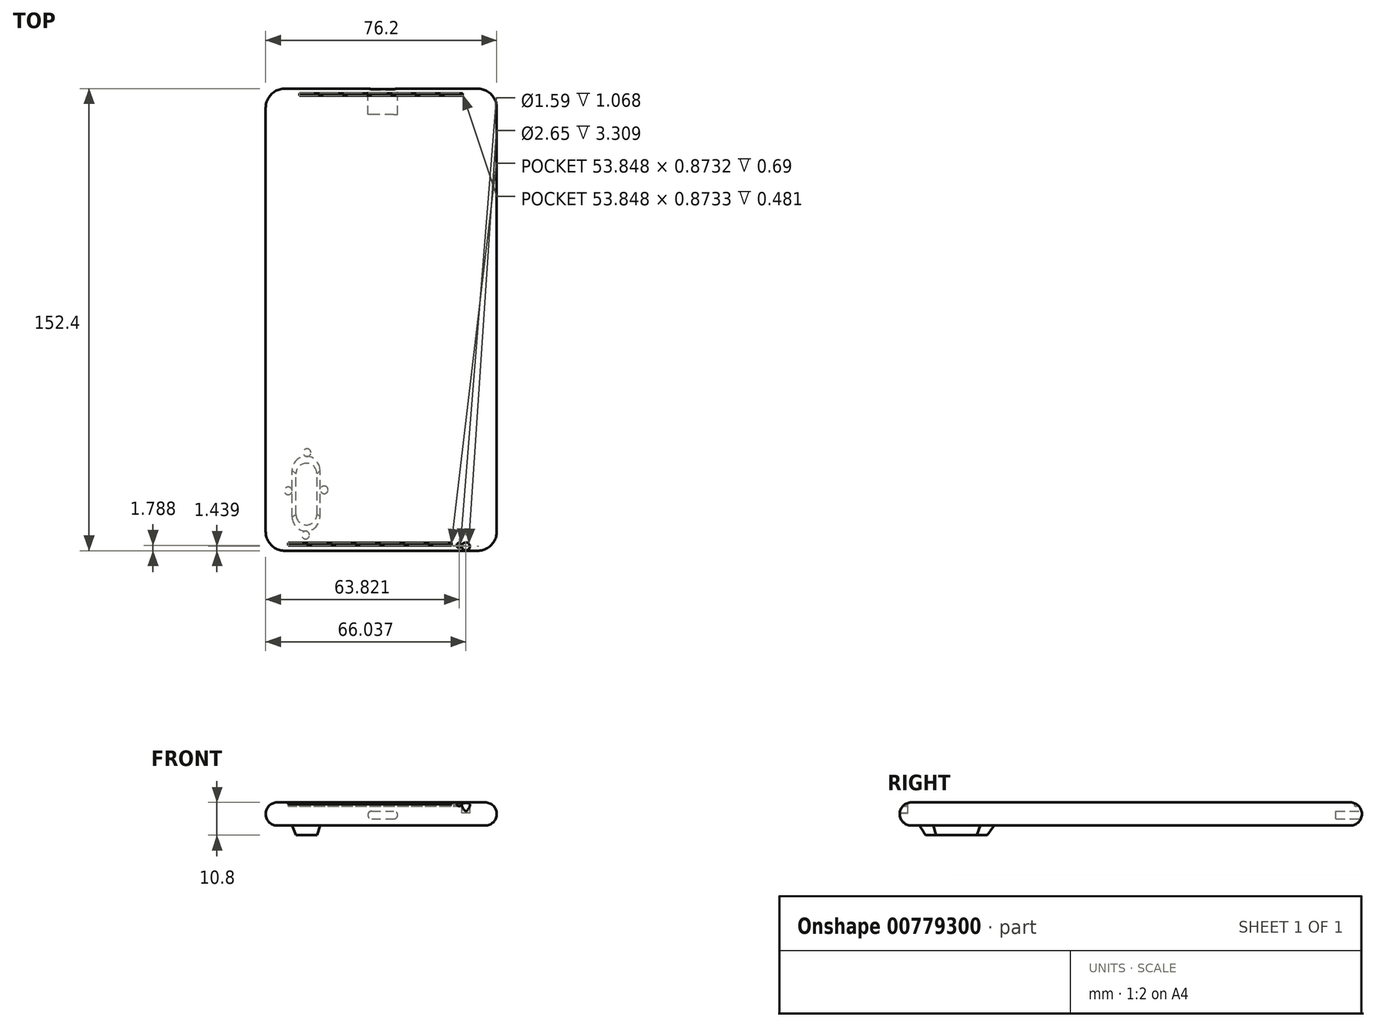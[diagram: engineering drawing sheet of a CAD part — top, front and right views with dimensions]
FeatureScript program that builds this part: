
annotation { "Feature Type Name" : "Feature", "Feature Type Description" : "" }
export const myFeature = defineFeature(function(context is Context, id is Id, definition is map)
    precondition{}
    {
        {
            var Q0;
            Q0=qCreatedBy(makeId("Top.planeOp"),FACE);
            var sketch = newSketch(context, id + "F0", { "sketchPlane" : qUnion([Q0])});
            skLineSegment(sketch, "E0.bottom", {"start": v(-50.31, -88.44) * mm, "end": v(25.89, -88.44) * mm});
            skLineSegment(sketch, "E0.top", {"start": v(-50.31, 63.96) * mm, "end": v(25.89, 63.96) * mm});
            skLineSegment(sketch, "E0.left", {"start": v(-50.31, -88.44) * mm, "end": v(-50.31, 63.96) * mm});
            skLineSegment(sketch, "E0.right", {"start": v(25.89, -88.44) * mm, "end": v(25.89, 63.96) * mm});
            skSolve(sketch);
        }
        {
            var Q0;
            Q0 = qSketchRegion(id + "F0", true);
            extrude(context, id + "F1", {"entities" : qUnion([Q0]), "depth" : 7.62 * mm, "offsetDistance" : 25.4 * mm});
        }
        {
            var Q0;
            Q0=makeQuery(id+"F1.opExtrude","CAP_FACE",FACE,{"disambiguationData":[OSD([sQuery(id+"F0.wireOp",EDGE,"E0.bottom"),sQuery(id+"F0.wireOp",EDGE,"E0.top"),sQuery(id+"F0.wireOp",EDGE,"E0.left"),sQuery(id+"F0.wireOp",EDGE,"E0.right")])],"isStart":false});
            var sketch = newSketch(context, id + "F2", { "sketchPlane" : qUnion([Q0])});
            skCircle(sketch, "E1", {"center": v(-43.96, 57.6) * mm, "radius": 6.35 * mm});
            skCircle(sketch, "E2", {"center": v(19.54, 57.6) * mm, "radius": 6.35 * mm});
            skCircle(sketch, "E3", {"center": v(-43.96, -82.1) * mm, "radius": 6.35 * mm});
            skCircle(sketch, "E4", {"center": v(19.54, -82.1) * mm, "radius": 6.35 * mm});
            skSolve(sketch);
        }
        {
            var Q0;
            {var subQ0=sQuery(id+"F2.wireOp",EDGE,"E4");var subQ1=makeQuery(id+"F1.opExtrude","CAP_EDGE",EDGE,{"disambiguationData":[OSD([sQuery(id+"F0.wireOp",EDGE,"E0.bottom")])],"isStart":false});var subQ2=makeQuery(id+"F2.imprint","INTERSECT",VERTEX,{"derivedFrom":[subQ1,subQ0]});Q0=makeQuery(id+"F2.imprint","IMPRINT",FACE,{"disambiguationData":[TD([[makeQuery(id+"F2.imprint","IMPRINT",EDGE,{"disambiguationData":[TD([[subQ2,-1.0]])],"derivedFrom":subQ0}),-1.0]])]});}
            var Q1;
            {var subQ0=sQuery(id+"F2.wireOp",EDGE,"E3");var subQ1=makeQuery(id+"F1.opExtrude","CAP_EDGE",EDGE,{"disambiguationData":[OSD([sQuery(id+"F0.wireOp",EDGE,"E0.bottom")])],"isStart":false});var subQ2=makeQuery(id+"F2.imprint","INTERSECT",VERTEX,{"derivedFrom":[subQ1,subQ0]});Q1=makeQuery(id+"F2.imprint","IMPRINT",FACE,{"disambiguationData":[TD([[makeQuery(id+"F2.imprint","IMPRINT",EDGE,{"disambiguationData":[TD([[subQ2,1.0]])],"derivedFrom":subQ0}),-1.0]])]});}
            var Q2;
            {var subQ0=sQuery(id+"F2.wireOp",EDGE,"E1");var subQ1=makeQuery(id+"F1.opExtrude","CAP_EDGE",EDGE,{"disambiguationData":[OSD([sQuery(id+"F0.wireOp",EDGE,"E0.top")])],"isStart":false});var subQ2=makeQuery(id+"F2.imprint","INTERSECT",VERTEX,{"derivedFrom":[subQ1,subQ0]});Q2=makeQuery(id+"F2.imprint","IMPRINT",FACE,{"disambiguationData":[TD([[makeQuery(id+"F2.imprint","IMPRINT",EDGE,{"disambiguationData":[TD([[subQ2,-1.0]])],"derivedFrom":subQ0}),-1.0]])]});}
            var Q3;
            {var subQ0=sQuery(id+"F2.wireOp",EDGE,"E2");var subQ1=makeQuery(id+"F1.opExtrude","CAP_EDGE",EDGE,{"disambiguationData":[OSD([sQuery(id+"F0.wireOp",EDGE,"E0.top")])],"isStart":false});var subQ2=makeQuery(id+"F2.imprint","INTERSECT",VERTEX,{"derivedFrom":[subQ1,subQ0]});Q3=makeQuery(id+"F2.imprint","IMPRINT",FACE,{"disambiguationData":[TD([[makeQuery(id+"F2.imprint","IMPRINT",EDGE,{"disambiguationData":[TD([[subQ2,1.0]])],"derivedFrom":subQ0}),-1.0]])]});}
            extrude(context, id + "F3", {"entities" : qUnion([Q0, Q1, Q2, Q3]), "operationType" : NewBodyOperationType.REMOVE, "oppositeDirection" : true, "depth" : 25.4 * mm, "offsetDistance" : 25.4 * mm});
        }
        {
            var Q0;
            Q0=makeQuery(id+"F1.opExtrude","CAP_EDGE",EDGE,{"disambiguationData":[OSD([sQuery(id+"F0.wireOp",EDGE,"E0.left")])],"isStart":false});
            fillet(context, id + "F4", {"entities" : qUnion([Q0]), "radius" : 3.8 * mm, "tangentPropagation" : true, "allowEdgeOverflow" : false});
        }
        {
            var Q0;
            Q0=makeQuery(id+"F1.opExtrude","CAP_EDGE",EDGE,{"disambiguationData":[OSD([sQuery(id+"F0.wireOp",EDGE,"E0.left")])],"isStart":true});
            fillet(context, id + "F5", {"entities" : qUnion([Q0]), "radius" : 3.8 * mm, "tangentPropagation" : true, "allowEdgeOverflow" : false});
        }
        {
            var Q0;
            Q0=makeQuery(id+"F1.opExtrude","CAP_FACE",FACE,{"disambiguationData":[OSD([sQuery(id+"F0.wireOp",EDGE,"E0.bottom"),sQuery(id+"F0.wireOp",EDGE,"E0.top"),sQuery(id+"F0.wireOp",EDGE,"E0.left"),sQuery(id+"F0.wireOp",EDGE,"E0.right")])],"isStart":true});
            var sketch = newSketch(context, id + "F6", { "sketchPlane" : qUnion([Q0])});
            skLineSegment(sketch, "E5.left", {"start": v(-41.57, 77.3) * mm, "end": v(-41.57, 61.91) * mm});
            skLineSegment(sketch, "E5.right", {"start": v(-32.36, 77.3) * mm, "end": v(-32.36, 61.91) * mm});
            skArc(sketch, "E6", {"start": v(-32.36, 77.3) * mm, "mid": v(-36.97, 81.91) * mm, "end": v(-41.57, 77.3) * mm});
            skArc(sketch, "E7", {"start": v(-41.57, 61.91) * mm, "mid": v(-36.97, 57.3) * mm, "end": v(-32.36, 61.91) * mm});
            skSolve(sketch);
        }
        {
            var Q0;
            Q0=qCreatedBy(makeId("Top.planeOp"),FACE);
            cPlane(context, id + "F7", {"entities" : qUnion([Q0]), "cplaneType" : CPlaneType.OFFSET, "offset" : 3.17 * mm, "oppositeDirection" : true, "width" : 152.4 * mm, "height" : 152.4 * mm});
        }
        {
            var Q0;
            Q0=qCreatedBy(id+"F7.planeOp",FACE);
            var sketch = newSketch(context, id + "F8", { "sketchPlane" : qUnion([Q0])});
            skLineSegment(sketch, "E8.left", {"start": v(-40.32, -76.45) * mm, "end": v(-40.32, -63.04) * mm});
            skLineSegment(sketch, "E8.right", {"start": v(-33.4, -76.45) * mm, "end": v(-33.4, -63.04) * mm});
            skArc(sketch, "E9", {"start": v(-40.32, -76.45) * mm, "mid": v(-36.85, -79.92) * mm, "end": v(-33.4, -76.45) * mm});
            skArc(sketch, "E10", {"start": v(-33.4, -63.04) * mm, "mid": v(-36.85, -59.58) * mm, "end": v(-40.32, -63.04) * mm});
            skSolve(sketch);
        }
        {
            var Q1;
            Q1=makeQuery(id+"F6.imprint","IMPRINT",FACE,{"disambiguationData":[TD([[makeQuery(id+"F6.imprint","IMPRINT",EDGE,{"derivedFrom":sQuery(id+"F6.wireOp",EDGE,"E5.left")}),1.0]])]});
            var Q2;
            Q2=makeQuery(id+"F8.imprint","IMPRINT",FACE,{"disambiguationData":[TD([[makeQuery(id+"F8.imprint","IMPRINT",EDGE,{"derivedFrom":sQuery(id+"F8.wireOp",EDGE,"E8.left")}),-1.0]])]});
            loft(context, id + "F9", {"operationType" : NewBodyOperationType.ADD, "sheetProfilesArray" : [{ "sheetProfileEntities" : qUnion([Q1]) }, { "sheetProfileEntities" : qUnion([Q2]) }]});
        }
        {
            var Q0;
            Q0=makeQuery(id+"F1.opExtrude","CAP_FACE",FACE,{"disambiguationData":[OSD([sQuery(id+"F0.wireOp",EDGE,"E0.bottom"),sQuery(id+"F0.wireOp",EDGE,"E0.top"),sQuery(id+"F0.wireOp",EDGE,"E0.left"),sQuery(id+"F0.wireOp",EDGE,"E0.right")])],"isStart":false});
            var sketch = newSketch(context, id + "F10", { "sketchPlane" : qUnion([Q0])});
            skLineSegment(sketch, "E11.bottom", {"start": v(-42.94, -85.64) * mm, "end": v(13.27, -85.64) * mm});
            skLineSegment(sketch, "E11.top", {"start": v(-42.94, -87.03) * mm, "end": v(13.27, -87.03) * mm});
            skLineSegment(sketch, "E11.left", {"start": v(-42.94, -85.64) * mm, "end": v(-42.94, -87.03) * mm});
            skLineSegment(sketch, "E11.right", {"start": v(13.27, -85.64) * mm, "end": v(13.27, -87.03) * mm});
            skCircle(sketch, "E12", {"center": v(16.81, -86.44) * mm, "radius": 1.62 * mm});
            skCircle(sketch, "E13", {"center": v(14.48, -86.38) * mm, "radius": 0.72 * mm});
            skSolve(sketch);
        }
        {
            var Q0;
            {var subQ0=sQuery(id+"F10.wireOp",EDGE,"E13");var subQ1=sQuery(id+"F10.wireOp",EDGE,"E12");var subQ2=makeQuery(id+"F10.imprint","INTERSECT",VERTEX,{"derivedFrom":[subQ1,subQ0]});Q0=qUnion([makeQuery(id+"F10.imprint","IMPRINT",FACE,{"disambiguationData":[TD([[makeQuery(id+"F10.imprint","IMPRINT",EDGE,{"derivedFrom":sQuery(id+"F10.wireOp",EDGE,"E11.bottom")}),-1.0]])]}),makeQuery(id+"F10.imprint","IMPRINT",FACE,{"disambiguationData":[TD([[makeQuery(id+"F10.imprint","IMPRINT",EDGE,{"disambiguationData":[TD([[subQ2,-1.0]])],"derivedFrom":subQ1}),1.0]])]}),makeQuery(id+"F10.imprint","IMPRINT",FACE,{"disambiguationData":[TD([[makeQuery(id+"F10.imprint","IMPRINT",EDGE,{"disambiguationData":[TD([[subQ2,-1.0]])],"derivedFrom":subQ0}),1.0]])]})]);}
            extrude(context, id + "F11", {"entities" : qUnion([Q0]), "operationType" : NewBodyOperationType.REMOVE, "endBound" : BoundingType.UP_TO_NEXT, "oppositeDirection" : true, "depth" : 0.5 * mm, "offsetDistance" : 25.4 * mm});
        }
        {
            var Q0;
            Q0=makeQuery(id+"F1.opExtrude","CAP_FACE",FACE,{"disambiguationData":[OSD([sQuery(id+"F0.wireOp",EDGE,"E0.bottom"),sQuery(id+"F0.wireOp",EDGE,"E0.top"),sQuery(id+"F0.wireOp",EDGE,"E0.left"),sQuery(id+"F0.wireOp",EDGE,"E0.right")])],"isStart":false});
            var sketch = newSketch(context, id + "F12", { "sketchPlane" : qUnion([Q0])});
            skLineSegment(sketch, "E14.bottom", {"start": v(-42.92, -85.78) * mm, "end": v(10.93, -85.78) * mm});
            skLineSegment(sketch, "E14.top", {"start": v(-42.92, -86.65) * mm, "end": v(10.93, -86.65) * mm});
            skLineSegment(sketch, "E14.left", {"start": v(-42.92, -85.78) * mm, "end": v(-42.92, -86.65) * mm});
            skLineSegment(sketch, "E14.right", {"start": v(10.93, -85.78) * mm, "end": v(10.93, -86.65) * mm});
            skCircle(sketch, "E15", {"center": v(13.51, -86.65) * mm, "radius": 0.8 * mm});
            skLineSegment(sketch, "E16.bottom", {"start": v(-39.13, 61.6) * mm, "end": v(14.71, 61.6) * mm});
            skLineSegment(sketch, "E16.top", {"start": v(-39.13, 62.47) * mm, "end": v(14.71, 62.47) * mm});
            skLineSegment(sketch, "E16.left", {"start": v(-39.13, 61.6) * mm, "end": v(-39.13, 62.47) * mm});
            skLineSegment(sketch, "E16.right", {"start": v(14.71, 61.6) * mm, "end": v(14.71, 62.47) * mm});
            skSolve(sketch);
        }
        {
            var Q0;
            Q0 = qSketchRegion(id + "F12", true);
            extrude(context, id + "F13", {"entities" : qUnion([Q0]), "operationType" : NewBodyOperationType.REMOVE, "oppositeDirection" : true, "depth" : 1.27 * mm, "offsetDistance" : 25.4 * mm});
        }
        {
            var Q0;
            Q0=makeQuery(id+"F1.opExtrude","CAP_FACE",FACE,{"disambiguationData":[OSD([sQuery(id+"F0.wireOp",EDGE,"E0.bottom"),sQuery(id+"F0.wireOp",EDGE,"E0.top"),sQuery(id+"F0.wireOp",EDGE,"E0.left"),sQuery(id+"F0.wireOp",EDGE,"E0.right")])],"isStart":false});
            var sketch = newSketch(context, id + "F14", { "sketchPlane" : qUnion([Q0])});
            skCircle(sketch, "E17", {"center": v(15.73, -87) * mm, "radius": 1.33 * mm});
            skSolve(sketch);
        }
        {
            var Q0;
            Q0=makeQuery(id+"F14.imprint","IMPRINT",FACE,{"disambiguationData":[TD([[makeQuery(id+"F14.imprint","IMPRINT",EDGE,{"derivedFrom":sQuery(id+"F14.wireOp",EDGE,"E17")}),1.0]])]});
            extrude(context, id + "F15", {"entities" : qUnion([Q0]), "operationType" : NewBodyOperationType.REMOVE, "oppositeDirection" : true, "depth" : 3.45 * mm, "offsetDistance" : 25.4 * mm});
        }
        {
            var Q0;
            Q0=qCreatedBy(makeId("Front.planeOp"),FACE);
            cPlane(context, id + "F16", {"entities" : qUnion([Q0]), "cplaneType" : CPlaneType.OFFSET, "offset" : 82.8 * mm, "oppositeDirection" : true, "width" : 152.4 * mm, "height" : 152.4 * mm});
        }
        {
            var Q0;
            Q0=qCreatedBy(id+"F16.planeOp",FACE);
            var sketch = newSketch(context, id + "F17", { "sketchPlane" : qUnion([Q0])});
            skLineSegment(sketch, "E18.bottom", {"start": v(-8.04, 4.73) * mm, "end": v(-15.33, 4.73) * mm});
            skLineSegment(sketch, "E18.top", {"start": v(-8.04, 2.2) * mm, "end": v(-15.33, 2.2) * mm});
            skArc(sketch, "E19", {"start": v(-8.04, 2.2) * mm, "mid": v(-6.78, 3.46) * mm, "end": v(-8.04, 4.73) * mm});
            skArc(sketch, "E20", {"start": v(-15.33, 4.73) * mm, "mid": v(-16.6, 3.46) * mm, "end": v(-15.33, 2.2) * mm});
            skPoint(sketch, "E21.centerSnap0", {"position": v(-6.78, 3.46) * mm});
            skPoint(sketch, "E21.center.orphan", {"position": v(14.73, 3.46) * mm});
            skSolve(sketch);
        }
        {
            var Q0;
            Q0=makeQuery(id+"F1.opExtrude","CAP_FACE",FACE,{"disambiguationData":[OSD([sQuery(id+"F0.wireOp",EDGE,"E0.bottom"),sQuery(id+"F0.wireOp",EDGE,"E0.top"),sQuery(id+"F0.wireOp",EDGE,"E0.left"),sQuery(id+"F0.wireOp",EDGE,"E0.right")])],"isStart":true});
            var sketch = newSketch(context, id + "F18", { "sketchPlane" : qUnion([Q0])});
            skCircle(sketch, "E22", {"center": v(-31, 68.35) * mm, "radius": 1.27 * mm});
            skCircle(sketch, "E23", {"center": v(-42.85, 68.68) * mm, "radius": 1.27 * mm});
            skCircle(sketch, "E24", {"center": v(-37.15, 83.27) * mm, "radius": 1.27 * mm});
            skCircle(sketch, "E25", {"center": v(-36.66, 56.08) * mm, "radius": 1.27 * mm});
            skSolve(sketch);
        }
        {
            var Q0;
            Q0 = qSketchRegion(id + "F18", true);
            extrude(context, id + "F19", {"entities" : qUnion([Q0]), "depth" : 0 * mm, "offsetDistance" : 25.4 * mm});
        }
        {
            var Q0;
            Q0 = qSketchRegion(id + "F17", true);
            extrude(context, id + "F20", {"entities" : qUnion([Q0]), "operationType" : NewBodyOperationType.REMOVE, "depth" : 27.43 * mm, "offsetDistance" : 25.4 * mm});
        }
    });
